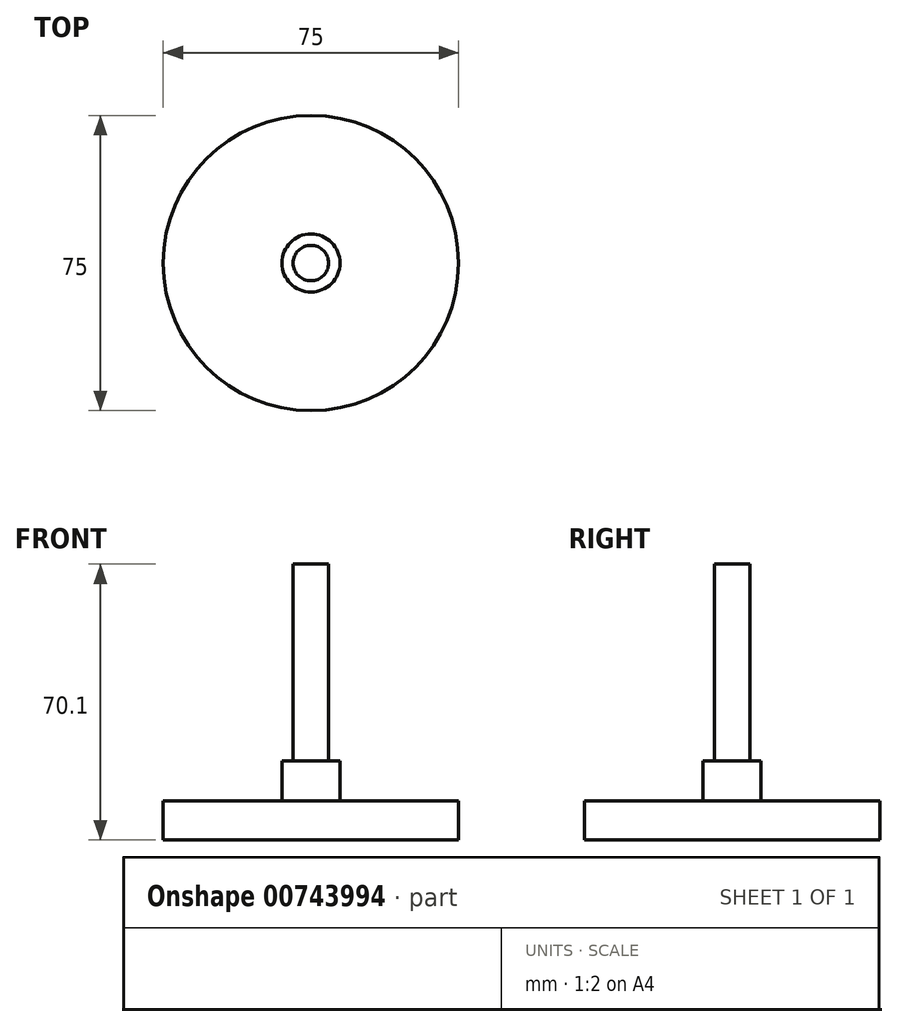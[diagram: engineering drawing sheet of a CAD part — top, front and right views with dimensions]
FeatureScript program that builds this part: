
annotation { "Feature Type Name" : "Feature", "Feature Type Description" : "" }
export const myFeature = defineFeature(function(context is Context, id is Id, definition is map)
    precondition{}
    {
        {
            var Q0;
            Q0=qCreatedBy(makeId("Top.planeOp"),FACE);
            var sketch = newSketch(context, id + "F0", { "sketchPlane" : qUnion([Q0])});
            skCircle(sketch, "E0", {"center": v(0, 0) * mm, "radius": 4.5 * mm});
            skSolve(sketch);
        }
        {
            var Q0;
            Q0=makeQuery(id+"F0.imprint","IMPRINT",FACE,{"disambiguationData":[TD([[makeQuery(id+"F0.imprint","IMPRINT",EDGE,{"derivedFrom":sQuery(id+"F0.wireOp",EDGE,"E0")}),1.0]])]});
            extrude(context, id + "F1", {"entities" : qUnion([Q0]), "depth" : 50 * mm, "offsetDistance" : 25 * mm});
        }
        {
            var Q0;
            Q0=qCreatedBy(makeId("Top.planeOp"),FACE);
            var sketch = newSketch(context, id + "F2", { "sketchPlane" : qUnion([Q0])});
            skCircle(sketch, "E1", {"center": v(0, 0) * mm, "radius": 7.38 * mm});
            skSolve(sketch);
        }
        {
            var Q0;
            Q0=makeQuery(id+"F2.imprint","IMPRINT",FACE,{"disambiguationData":[TD([[makeQuery(id+"F2.imprint","IMPRINT",EDGE,{"derivedFrom":sQuery(id+"F2.wireOp",EDGE,"E1")}),1.0]])]});
            extrude(context, id + "F3", {"entities" : qUnion([Q0]), "operationType" : NewBodyOperationType.ADD, "oppositeDirection" : true, "depth" : 10.1 * mm, "offsetDistance" : 25 * mm});
        }
        {
            var Q0;
            Q0=makeQuery(id+"F3.opExtrude","CAP_FACE",FACE,{"disambiguationData":[OSD([sQuery(id+"F2.wireOp",EDGE,"E1")])],"isStart":false});
            var sketch = newSketch(context, id + "F4", { "sketchPlane" : qUnion([Q0])});
            skCircle(sketch, "E2", {"center": v(0, 0) * mm, "radius": 37.5 * mm});
            skSolve(sketch);
        }
        {
            var Q0;
            Q0 = qSketchRegion(id + "F4", true);
            extrude(context, id + "F5", {"entities" : qUnion([Q0]), "operationType" : NewBodyOperationType.ADD, "depth" : 10 * mm, "offsetDistance" : 25 * mm});
        }
    });
